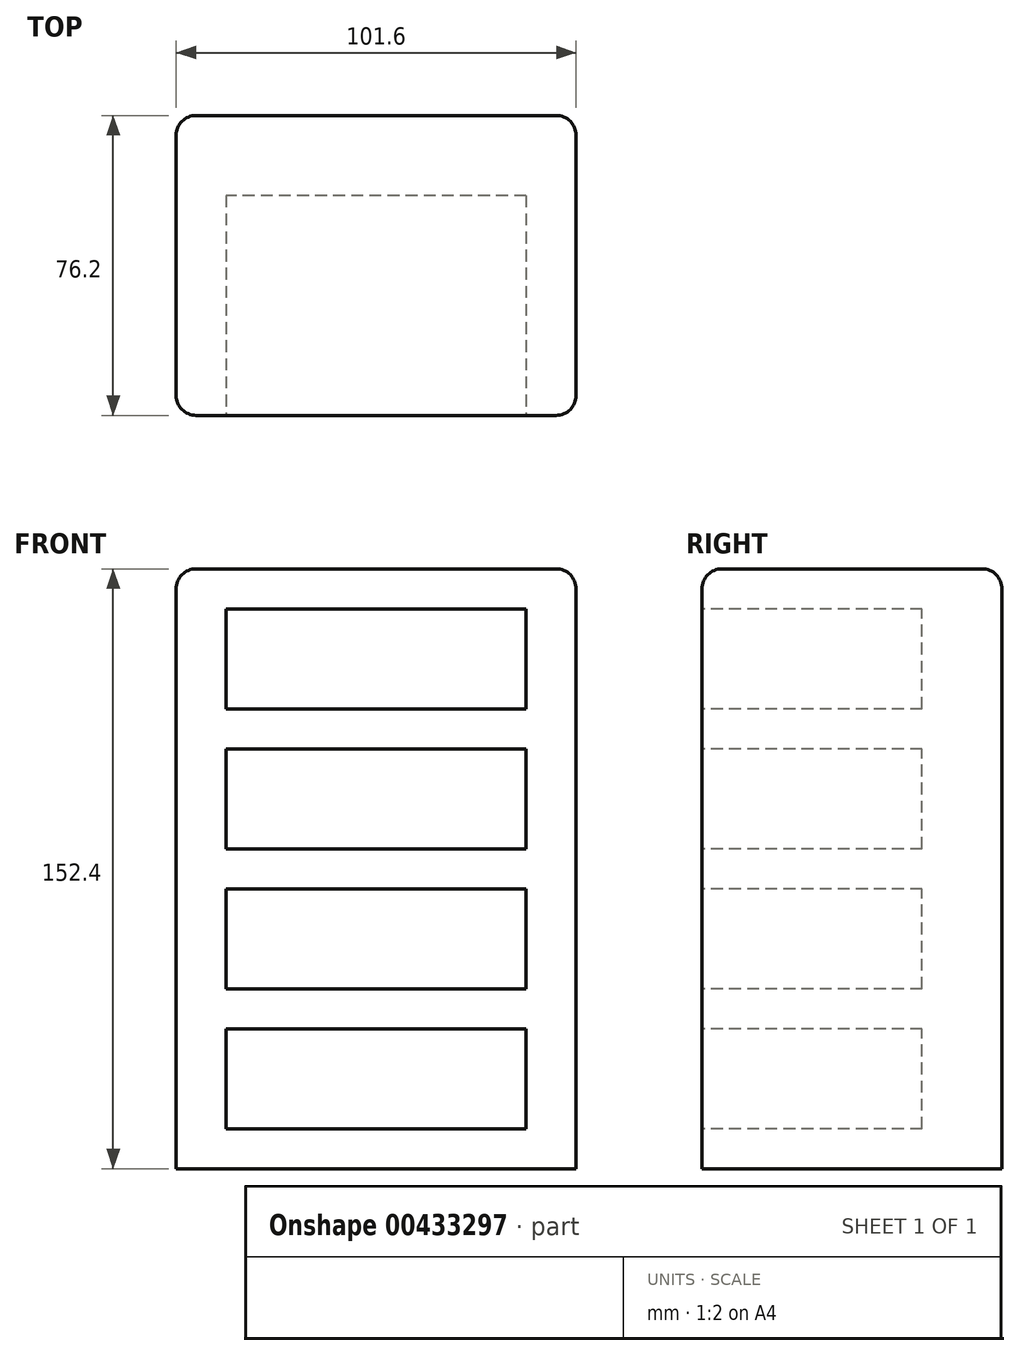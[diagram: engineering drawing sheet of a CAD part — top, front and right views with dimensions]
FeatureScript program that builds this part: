
annotation { "Feature Type Name" : "Feature", "Feature Type Description" : "" }
export const myFeature = defineFeature(function(context is Context, id is Id, definition is map)
    precondition{}
    {
        {
            var Q0;
            Q0=qCreatedBy(makeId("Top.planeOp"),FACE);
            var sketch = newSketch(context, id + "F0", { "sketchPlane" : qUnion([Q0])});
            skLineSegment(sketch, "E0.bottom", {"start": v(50.8, -38.1) * mm, "end": v(-50.8, -38.1) * mm});
            skLineSegment(sketch, "E0.top", {"start": v(50.8, 38.1) * mm, "end": v(-50.8, 38.1) * mm});
            skLineSegment(sketch, "E0.left", {"start": v(50.8, -38.1) * mm, "end": v(50.8, 38.1) * mm});
            skLineSegment(sketch, "E0.right", {"start": v(-50.8, -38.1) * mm, "end": v(-50.8, 38.1) * mm});
            skPoint(sketch, "E0.middle", {"position": v(0, 0) * mm});
            skSolve(sketch);
        }
        {
            var Q0;
            Q0 = qSketchRegion(id + "F0", true);
            extrude(context, id + "F1", {"entities" : qUnion([Q0]), "depth" : 152.4 * mm});
        }
        {
            var Q0;
            Q0=makeQuery(id+"F1.opExtrude","SWEPT_FACE",FACE,{"disambiguationData":[OSD([sQuery(id+"F0.wireOp",EDGE,"E0.bottom")])]});
            var sketch = newSketch(context, id + "F2", { "sketchPlane" : qUnion([Q0])});
            skLineSegment(sketch, "E1.bottom", {"start": v(38.1, 116.84) * mm, "end": v(-38.1, 116.84) * mm});
            skLineSegment(sketch, "E1.top", {"start": v(38.1, 142.24) * mm, "end": v(-38.1, 142.24) * mm});
            skLineSegment(sketch, "E1.left", {"start": v(38.1, 116.84) * mm, "end": v(38.1, 142.24) * mm});
            skLineSegment(sketch, "E1.right", {"start": v(-38.1, 116.84) * mm, "end": v(-38.1, 142.24) * mm});
            skPoint(sketch, "E1.middle", {"position": v(0, 129.54) * mm});
            skLineSegment(sketch, "E2.0.1.0", {"start": v(38.1, 106.68) * mm, "end": v(-38.1, 106.68) * mm});
            skLineSegment(sketch, "E2.0.1.1", {"start": v(-38.1, 81.28) * mm, "end": v(-38.1, 106.68) * mm});
            skLineSegment(sketch, "E2.0.1.2", {"start": v(38.1, 81.28) * mm, "end": v(-38.1, 81.28) * mm});
            skLineSegment(sketch, "E2.0.1.3", {"start": v(38.1, 81.28) * mm, "end": v(38.1, 106.68) * mm});
            skLineSegment(sketch, "E2.0.2.0", {"start": v(38.1, 71.12) * mm, "end": v(-38.1, 71.12) * mm});
            skLineSegment(sketch, "E2.0.2.1", {"start": v(-38.1, 45.72) * mm, "end": v(-38.1, 71.12) * mm});
            skLineSegment(sketch, "E2.0.2.2", {"start": v(38.1, 45.72) * mm, "end": v(-38.1, 45.72) * mm});
            skLineSegment(sketch, "E2.0.2.3", {"start": v(38.1, 45.72) * mm, "end": v(38.1, 71.12) * mm});
            skLineSegment(sketch, "E2.0.3.0", {"start": v(38.1, 35.56) * mm, "end": v(-38.1, 35.56) * mm});
            skLineSegment(sketch, "E2.0.3.1", {"start": v(-38.1, 10.16) * mm, "end": v(-38.1, 35.56) * mm});
            skLineSegment(sketch, "E2.0.3.2", {"start": v(38.1, 10.16) * mm, "end": v(-38.1, 10.16) * mm});
            skLineSegment(sketch, "E2.0.3.3", {"start": v(38.1, 10.16) * mm, "end": v(38.1, 35.56) * mm});
            skLineSegment(sketch, "E2.direction1", {"start": v(-38.1, 142.24) * mm, "end": v(-37.6, 142.24) * mm, "construction": true});
            skLineSegment(sketch, "E2.direction2", {"start": v(-38.1, 142.24) * mm, "end": v(-38.1, 106.68) * mm, "construction": true});
            skSolve(sketch);
        }
        {
            var Q0;
            Q0=makeQuery(id+"F2.imprint","IMPRINT",FACE,{"disambiguationData":[TD([[makeQuery(id+"F2.imprint","IMPRINT",EDGE,{"derivedFrom":sQuery(id+"F2.wireOp",EDGE,"E1.bottom")}),-1.0]])]});
            var Q1;
            Q1=makeQuery(id+"F2.imprint","IMPRINT",FACE,{"disambiguationData":[TD([[makeQuery(id+"F2.imprint","IMPRINT",EDGE,{"derivedFrom":sQuery(id+"F2.wireOp",EDGE,"E2.0.1.0")}),1.0]])]});
            var Q2;
            Q2=makeQuery(id+"F2.imprint","IMPRINT",FACE,{"disambiguationData":[TD([[makeQuery(id+"F2.imprint","IMPRINT",EDGE,{"derivedFrom":sQuery(id+"F2.wireOp",EDGE,"E2.0.2.0")}),1.0]])]});
            var Q3;
            Q3=makeQuery(id+"F2.imprint","IMPRINT",FACE,{"disambiguationData":[TD([[makeQuery(id+"F2.imprint","IMPRINT",EDGE,{"derivedFrom":sQuery(id+"F2.wireOp",EDGE,"E2.0.3.0")}),1.0]])]});
            extrude(context, id + "F3", {"entities" : qUnion([Q0, Q1, Q2, Q3]), "operationType" : NewBodyOperationType.REMOVE, "oppositeDirection" : true, "depth" : 55.88 * mm});
        }
        {
            var Q0;
            Q0=makeQuery(id+"F1.opExtrude","CAP_EDGE",EDGE,{"disambiguationData":[OSD([sQuery(id+"F0.wireOp",EDGE,"E0.left")])],"isStart":false});
            var Q1;
            Q1=makeQuery(id+"F1.opExtrude","CAP_EDGE",EDGE,{"disambiguationData":[OSD([sQuery(id+"F0.wireOp",EDGE,"E0.right")])],"isStart":false});
            var Q2;
            Q2=makeQuery(id+"F1.opExtrude","CAP_EDGE",EDGE,{"disambiguationData":[OSD([sQuery(id+"F0.wireOp",EDGE,"E0.bottom")])],"isStart":false});
            var Q3;
            Q3=makeQuery(id+"F1.opExtrude","CAP_EDGE",EDGE,{"disambiguationData":[OSD([sQuery(id+"F0.wireOp",EDGE,"E0.top")])],"isStart":false});
            var Q4;
            Q4=makeQuery(id+"F1.opExtrude","SWEPT_EDGE",EDGE,{"disambiguationData":[OSD([sQuery(id+"F0.wireOp",EDGE,"E0.bottom"),sQuery(id+"F0.wireOp",EDGE,"E0.left")])]});
            var Q5;
            Q5=makeQuery(id+"F1.opExtrude","SWEPT_EDGE",EDGE,{"disambiguationData":[OSD([sQuery(id+"F0.wireOp",EDGE,"E0.top"),sQuery(id+"F0.wireOp",EDGE,"E0.left")])]});
            var Q6;
            Q6=makeQuery(id+"F1.opExtrude","SWEPT_EDGE",EDGE,{"disambiguationData":[OSD([sQuery(id+"F0.wireOp",EDGE,"E0.bottom"),sQuery(id+"F0.wireOp",EDGE,"E0.right")])]});
            var Q7;
            Q7=makeQuery(id+"F1.opExtrude","SWEPT_EDGE",EDGE,{"disambiguationData":[OSD([sQuery(id+"F0.wireOp",EDGE,"E0.top"),sQuery(id+"F0.wireOp",EDGE,"E0.right")])]});
            fillet(context, id + "F4", {"entities" : qUnion([Q0, Q1, Q2, Q3, Q4, Q5, Q6, Q7]), "radius" : 5.08 * mm, "tangentPropagation" : true, "allowEdgeOverflow" : false});
        }
    });
